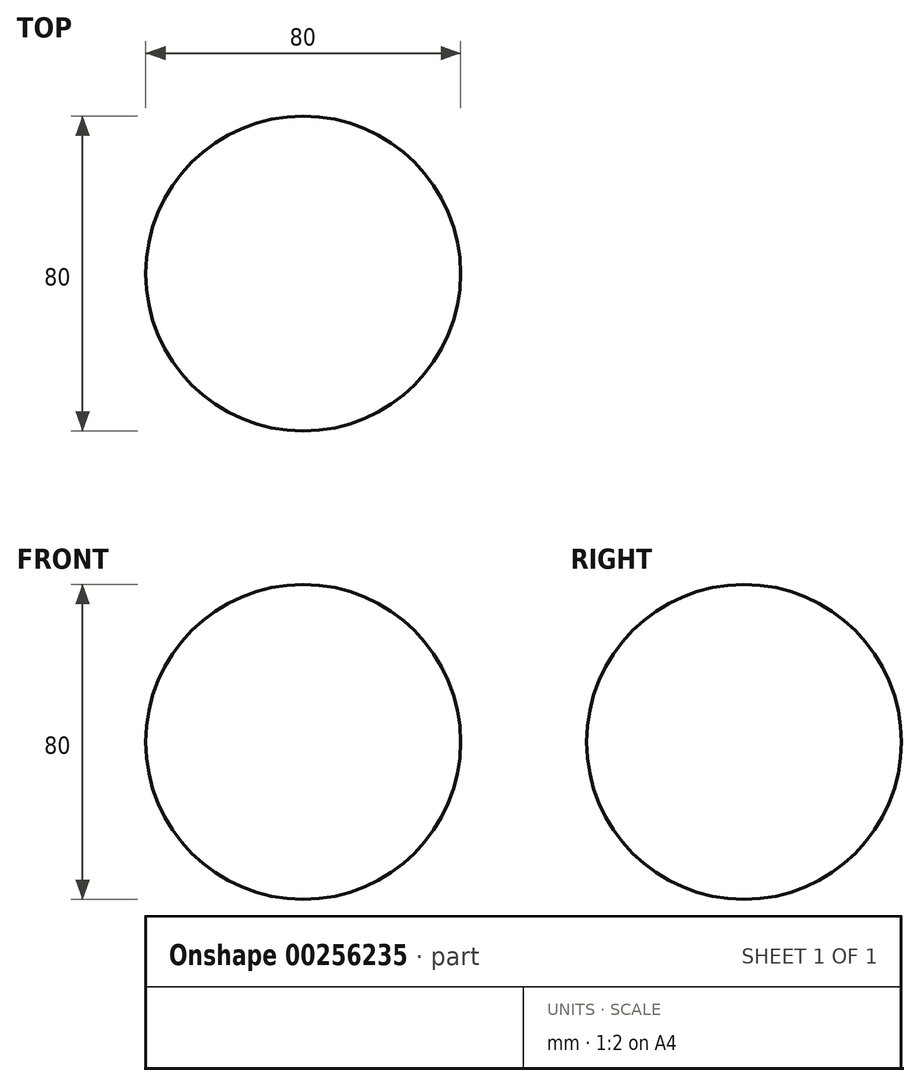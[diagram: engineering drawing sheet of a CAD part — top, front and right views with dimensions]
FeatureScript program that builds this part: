
annotation { "Feature Type Name" : "Feature", "Feature Type Description" : "" }
export const myFeature = defineFeature(function(context is Context, id is Id, definition is map)
    precondition{}
    {
        {
            var Q0;
            Q0=qCreatedBy(makeId("Front.planeOp"),FACE);
            var sketch = newSketch(context, id + "F0", { "sketchPlane" : qUnion([Q0])});
            skArc(sketch, "E0", {"start": v(0, 40) * mm, "mid": v(40, 0) * mm, "end": v(0, -40) * mm});
            skLineSegment(sketch, "E1", {"start": v(0, 0) * mm, "end": v(0, 56.66) * mm});
            skLineSegment(sketch, "E2", {"start": v(0, 56.66) * mm, "end": v(0, -52.07) * mm, "construction": true});
            skSolve(sketch);
        }
        {
            var Q0;
            Q0=sQuery(id+"F0.wireOp",EDGE,"E0");
            var Q1;
            Q1=sQuery(id+"F0.wireOp",EDGE,"E2");
            revolve(context, id + "F1", {"bodyType" : ToolBodyType.SURFACE, "surfaceEntities" : qUnion([Q0]), "axis" : qUnion([Q1]), "revolveType" : RevolveType.FULL});
        }
    });
